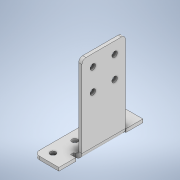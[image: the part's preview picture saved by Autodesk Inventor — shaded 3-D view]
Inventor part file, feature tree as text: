
AUTODESK INVENTOR PART (.ipt)
format: ipt  version: 2020 (Build 240168000, 168)  size: 239,616 bytes
history: native  units: mm
features: sketch x4, sheet_metal_op x2, hole x2, chamfer x2, other x2
ambient origin geometry x8: Origin, YZ Plane, XZ Plane, XY Plane, X Axis, Y Axis, Z Axis, Center Point
bodies: Solid1 (feature_tree)
feature tree (12):
  sheet_metal_op  "Face1"
  sheet_metal_op  "Fold1"
  hole  "Hole1"  [1 undecoded]
  hole  "Hole2"  [1 undecoded]
  chamfer  "Corner Round1"
  chamfer  "Corner Round2"
  sketch  "Sketch2"  dims[d7=3.0mm d8=3.0mm]
  other  "Plate1"
  sketch  "Sketch3"  dims[d9=1.5mm d10=6.0mm]
  sketch  "Sketch4"  dims[d11=3.0mm]
  sketch  "Sketch5"  dims[d12=90.0deg d13=3.0mm d14=5.1mm d15=5.1mm d16=5.1mm d17=5.1mm d18=14.0mm d19=14.0mm d20=14.0mm d21=14.0mm d22=10.0mm d23=10.0mm d24=30.0mm d25=30.0mm d26=5.1mm d27=6.0mm d28=4.0mm d29=2.0mm d30=90.0deg d31=3.0mm d32=20.594885mm d33=5.1mm d34=5.1mm d35=5.1mm d36=5.1mm d37=70.0mm d38=10.0mm d39=10.0mm d40=10.0mm d41=10.0mm d42=70.0mm d43=50.0mm d44=50.0mm d45=5.1mm d46=6.0mm d47=4.0mm d48=2.0mm d49=90.0deg d50=3.0mm d51=20.594885mm d52=3.7mm d53=4.64mm d54=22.58mm d55=77.15mm d56=18.575mm d57=18.575mm d58=20.0mm d59=20.0mm d60=78.0mm]
  other  "Definition1"
note: 2 required parameter values undecoded (feature->parameter linkage not recoverable at this tier; creation-order binding heuristic only, values carry confidence <= 0.55)
